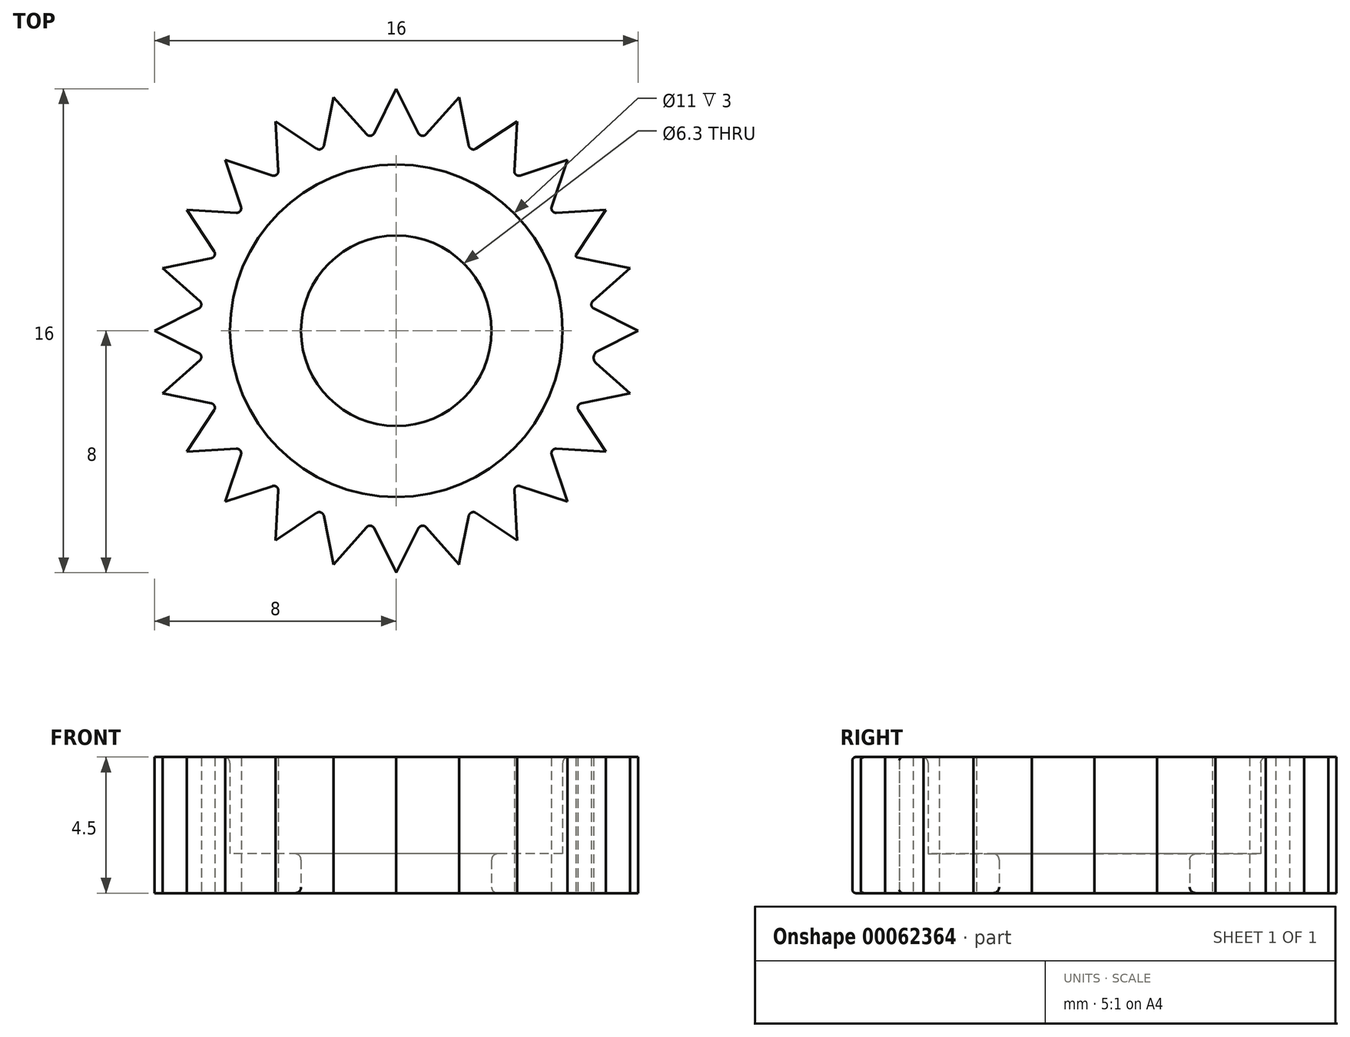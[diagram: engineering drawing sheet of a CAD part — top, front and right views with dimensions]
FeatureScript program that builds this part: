
annotation { "Feature Type Name" : "Feature", "Feature Type Description" : "" }
export const myFeature = defineFeature(function(context is Context, id is Id, definition is map)
    precondition{}
    {
        {
            var Q0;
            Q0=qCreatedBy(makeId("Top.planeOp"),FACE);
            var sketch = newSketch(context, id + "F0", { "sketchPlane" : qUnion([Q0])});
            skCircle(sketch, "E0", {"center": v(0, 0) * mm, "radius": 8 * mm, "construction": true});
            skCircle(sketch, "E1", {"center": v(0, 0) * mm, "radius": 6.5 * mm, "construction": true});
            skCircle(sketch, "E2", {"center": v(0, 0) * mm, "radius": 5.5 * mm});
            skCircle(sketch, "E3", {"center": v(0, 0) * mm, "radius": 3.15 * mm});
            skLineSegment(sketch, "E4", {"start": v(0, 6.5) * mm, "end": v(0.75, 6.5) * mm, "construction": true});
            skLineSegment(sketch, "E5", {"start": v(0.73, 6.53) * mm, "end": v(0, 8) * mm});
            skLineSegment(sketch, "E6", {"start": v(0, 8) * mm, "end": v(0, 6.5) * mm, "construction": true});
            skLineSegment(sketch, "E7.MirrorCS", {"start": v(-0.73, 6.53) * mm, "end": v(0, 8) * mm});
            skPoint(sketch, "E8.visualSharp", {"position": v(0, 8) * mm});
            skLineSegment(sketch, "E9.1.0", {"start": v(2.4, 6.12) * mm, "end": v(2.07, 7.73) * mm});
            skLineSegment(sketch, "E9.1.2", {"start": v(0.98, 6.5) * mm, "end": v(2.07, 7.73) * mm});
            skLineSegment(sketch, "E9.2.0", {"start": v(3.9, 5.29) * mm, "end": v(4, 6.93) * mm});
            skLineSegment(sketch, "E9.2.2", {"start": v(2.63, 6.02) * mm, "end": v(4, 6.93) * mm});
            skLineSegment(sketch, "E9.3.0", {"start": v(5.14, 4.1) * mm, "end": v(5.66, 5.66) * mm});
            skLineSegment(sketch, "E9.3.2", {"start": v(4.1, 5.14) * mm, "end": v(5.66, 5.66) * mm});
            skLineSegment(sketch, "E9.4.0", {"start": v(5.94, 2.5) * mm, "end": v(6.93, 4) * mm});
            skLineSegment(sketch, "E9.4.2", {"start": v(5.29, 3.9) * mm, "end": v(6.93, 4) * mm});
            skLineSegment(sketch, "E9.5.0", {"start": v(6.5, 0.98) * mm, "end": v(7.73, 2.07) * mm});
            skLineSegment(sketch, "E9.5.1", {"start": v(7.5, 1.87) * mm, "end": v(7.5, 1.87) * mm});
            skLineSegment(sketch, "E9.5.2", {"start": v(5.97, 2.43) * mm, "end": v(7.73, 2.07) * mm});
            skLineSegment(sketch, "E9.6.0", {"start": v(6.66, -0.67) * mm, "end": v(8, 0) * mm});
            skLineSegment(sketch, "E9.6.1", {"start": v(7.73, -0.13) * mm, "end": v(7.73, -0.13) * mm});
            skLineSegment(sketch, "E9.6.2", {"start": v(6.53, 0.73) * mm, "end": v(8, 0) * mm});
            skLineSegment(sketch, "E9.7.0", {"start": v(6.12, -2.4) * mm, "end": v(7.73, -2.07) * mm});
            skLineSegment(sketch, "E9.7.2", {"start": v(6.6, -1.08) * mm, "end": v(7.73, -2.07) * mm});
            skLineSegment(sketch, "E9.8.0", {"start": v(5.29, -3.9) * mm, "end": v(6.93, -4) * mm});
            skLineSegment(sketch, "E9.8.2", {"start": v(6.02, -2.63) * mm, "end": v(6.93, -4) * mm});
            skLineSegment(sketch, "E9.9.0", {"start": v(4.1, -5.14) * mm, "end": v(5.66, -5.66) * mm});
            skLineSegment(sketch, "E9.9.2", {"start": v(5.14, -4.1) * mm, "end": v(5.66, -5.66) * mm});
            skLineSegment(sketch, "E9.10.0", {"start": v(2.63, -6.02) * mm, "end": v(4, -6.93) * mm});
            skLineSegment(sketch, "E9.10.2", {"start": v(3.9, -5.29) * mm, "end": v(4, -6.93) * mm});
            skLineSegment(sketch, "E9.11.0", {"start": v(0.98, -6.5) * mm, "end": v(2.07, -7.73) * mm});
            skLineSegment(sketch, "E9.11.2", {"start": v(2.4, -6.12) * mm, "end": v(2.07, -7.73) * mm});
            skLineSegment(sketch, "E9.12.0", {"start": v(-0.73, -6.53) * mm, "end": v(0, -8) * mm});
            skLineSegment(sketch, "E9.12.1", {"start": v(-0.13, -7.73) * mm, "end": v(-0.13, -7.73) * mm});
            skLineSegment(sketch, "E9.12.2", {"start": v(0.73, -6.53) * mm, "end": v(0, -8) * mm});
            skLineSegment(sketch, "E9.13.0", {"start": v(-2.4, -6.12) * mm, "end": v(-2.07, -7.73) * mm});
            skLineSegment(sketch, "E9.13.2", {"start": v(-0.98, -6.5) * mm, "end": v(-2.07, -7.73) * mm});
            skLineSegment(sketch, "E9.14.0", {"start": v(-3.9, -5.29) * mm, "end": v(-4, -6.93) * mm});
            skLineSegment(sketch, "E9.14.2", {"start": v(-2.63, -6.02) * mm, "end": v(-4, -6.93) * mm});
            skLineSegment(sketch, "E9.15.0", {"start": v(-5.14, -4.1) * mm, "end": v(-5.66, -5.66) * mm});
            skLineSegment(sketch, "E9.15.2", {"start": v(-4.1, -5.14) * mm, "end": v(-5.66, -5.66) * mm});
            skLineSegment(sketch, "E9.16.0", {"start": v(-6.02, -2.63) * mm, "end": v(-6.93, -4) * mm});
            skLineSegment(sketch, "E9.16.1", {"start": v(-6.76, -3.75) * mm, "end": v(-6.76, -3.75) * mm});
            skLineSegment(sketch, "E9.16.2", {"start": v(-5.29, -3.9) * mm, "end": v(-6.93, -4) * mm});
            skLineSegment(sketch, "E9.17.0", {"start": v(-6.5, -0.98) * mm, "end": v(-7.73, -2.07) * mm});
            skLineSegment(sketch, "E9.17.1", {"start": v(-7.5, -1.87) * mm, "end": v(-7.5, -1.87) * mm});
            skLineSegment(sketch, "E9.17.2", {"start": v(-6.12, -2.4) * mm, "end": v(-7.73, -2.07) * mm});
            skLineSegment(sketch, "E9.18.0", {"start": v(-6.53, 0.73) * mm, "end": v(-8, 0) * mm});
            skLineSegment(sketch, "E9.18.2", {"start": v(-6.53, -0.73) * mm, "end": v(-8, 0) * mm});
            skLineSegment(sketch, "E9.19.0", {"start": v(-6.12, 2.4) * mm, "end": v(-7.73, 2.07) * mm});
            skLineSegment(sketch, "E9.19.2", {"start": v(-6.5, 0.98) * mm, "end": v(-7.73, 2.07) * mm});
            skLineSegment(sketch, "E9.20.0", {"start": v(-5.29, 3.9) * mm, "end": v(-6.93, 4) * mm});
            skLineSegment(sketch, "E9.20.2", {"start": v(-6.02, 2.63) * mm, "end": v(-6.93, 4) * mm});
            skLineSegment(sketch, "E9.21.0", {"start": v(-4.1, 5.14) * mm, "end": v(-5.66, 5.66) * mm});
            skLineSegment(sketch, "E9.21.2", {"start": v(-5.14, 4.1) * mm, "end": v(-5.66, 5.66) * mm});
            skLineSegment(sketch, "E9.22.0", {"start": v(-2.63, 6.02) * mm, "end": v(-4, 6.93) * mm});
            skLineSegment(sketch, "E9.22.2", {"start": v(-3.9, 5.29) * mm, "end": v(-4, 6.93) * mm});
            skLineSegment(sketch, "E9.23.0", {"start": v(-0.98, 6.5) * mm, "end": v(-2.07, 7.73) * mm});
            skLineSegment(sketch, "E9.23.2", {"start": v(-2.4, 6.12) * mm, "end": v(-2.07, 7.73) * mm});
            skLineSegment(sketch, "E9.anchor1", {"start": v(0, 0) * mm, "end": v(0.75, 6.5) * mm, "construction": true});
            skLineSegment(sketch, "E9.anchor2", {"start": v(0, 0) * mm, "end": v(-0.96, 6.47) * mm, "construction": true});
            skPoint(sketch, "E10.newPointA", {"position": v(0.75, 6.5) * mm});
            skPoint(sketch, "E10.newPointB", {"position": v(0.96, 6.47) * mm});
            skArc(sketch, "E10.filletArc", {"start": v(0.73, 6.53) * mm, "mid": v(0.85, 6.45) * mm, "end": v(0.98, 6.5) * mm});
            skPoint(sketch, "E11.newPointA", {"position": v(2.4, 6.08) * mm});
            skPoint(sketch, "E11.newPointB", {"position": v(2.6, 6) * mm});
            skArc(sketch, "E11.filletArc", {"start": v(2.4, 6.12) * mm, "mid": v(2.49, 6) * mm, "end": v(2.63, 6.02) * mm});
            skPoint(sketch, "E12.newPointA", {"position": v(3.9, 5.25) * mm});
            skPoint(sketch, "E12.newPointB", {"position": v(4.07, 5.13) * mm});
            skArc(sketch, "E12.filletArc", {"start": v(3.9, 5.29) * mm, "mid": v(3.96, 5.16) * mm, "end": v(4.1, 5.14) * mm});
            skPoint(sketch, "E13.newPointA", {"position": v(5.25, 3.9) * mm});
            skPoint(sketch, "E13.newPointB", {"position": v(5.13, 4.07) * mm});
            skArc(sketch, "E13.filletArc", {"start": v(5.14, 4.1) * mm, "mid": v(5.16, 3.96) * mm, "end": v(5.29, 3.9) * mm});
            skPoint(sketch, "E14.newPointA", {"position": v(6, 2.6) * mm});
            skPoint(sketch, "E14.newPointB", {"position": v(6.08, 2.4) * mm});
            skArc(sketch, "E14.filletArc", {"start": v(5.94, 2.5) * mm, "mid": v(5.94, 2.46) * mm, "end": v(5.97, 2.43) * mm});
            skPoint(sketch, "E15.newPointA", {"position": v(6.47, 0.96) * mm});
            skPoint(sketch, "E15.newPointB", {"position": v(6.5, 0.75) * mm});
            skArc(sketch, "E15.filletArc", {"start": v(6.5, 0.98) * mm, "mid": v(6.45, 0.85) * mm, "end": v(6.53, 0.73) * mm});
            skPoint(sketch, "E16.newPointA", {"position": v(6.5, -0.75) * mm});
            skPoint(sketch, "E16.newPointB", {"position": v(6.47, -0.96) * mm});
            skArc(sketch, "E16.filletArc", {"start": v(6.66, -0.67) * mm, "mid": v(6.53, -0.86) * mm, "end": v(6.6, -1.08) * mm});
            skPoint(sketch, "E17.newPointA", {"position": v(6.08, -2.4) * mm});
            skPoint(sketch, "E17.newPointB", {"position": v(6, -2.6) * mm});
            skArc(sketch, "E17.filletArc", {"start": v(6.12, -2.4) * mm, "mid": v(6, -2.49) * mm, "end": v(6.02, -2.63) * mm});
            skPoint(sketch, "E18.newPointA", {"position": v(5.56, -5.37) * mm});
            skPoint(sketch, "E18.newPointB", {"position": v(5.37, -5.56) * mm});
            skPoint(sketch, "E19.newPointA", {"position": v(2.6, -6) * mm});
            skPoint(sketch, "E19.newPointB", {"position": v(2.4, -6.08) * mm});
            skArc(sketch, "E19.filletArc", {"start": v(2.63, -6.02) * mm, "mid": v(2.49, -6) * mm, "end": v(2.4, -6.12) * mm});
            skPoint(sketch, "E20.newPointA", {"position": v(0.75, -6.5) * mm});
            skPoint(sketch, "E20.newPointB", {"position": v(0.96, -6.47) * mm});
            skArc(sketch, "E20.filletArc", {"start": v(0.98, -6.5) * mm, "mid": v(0.85, -6.45) * mm, "end": v(0.73, -6.53) * mm});
            skPoint(sketch, "E21.newPointA", {"position": v(3.9, -5.25) * mm});
            skPoint(sketch, "E21.newPointB", {"position": v(4.07, -5.13) * mm});
            skArc(sketch, "E21.filletArc", {"start": v(4.1, -5.14) * mm, "mid": v(3.96, -5.16) * mm, "end": v(3.9, -5.29) * mm});
            skPoint(sketch, "E22.newPointA", {"position": v(-0.96, -6.47) * mm});
            skPoint(sketch, "E22.newPointB", {"position": v(-0.75, -6.5) * mm});
            skArc(sketch, "E22.filletArc", {"start": v(-0.73, -6.53) * mm, "mid": v(-0.85, -6.45) * mm, "end": v(-0.98, -6.5) * mm});
            skPoint(sketch, "E23.newPointA", {"position": v(-2.6, -6) * mm});
            skPoint(sketch, "E23.newPointB", {"position": v(-2.4, -6.08) * mm});
            skArc(sketch, "E23.filletArc", {"start": v(-2.4, -6.12) * mm, "mid": v(-2.49, -6) * mm, "end": v(-2.63, -6.02) * mm});
            skPoint(sketch, "E24.newPointA", {"position": v(-4.07, -5.13) * mm});
            skPoint(sketch, "E24.newPointB", {"position": v(-3.9, -5.25) * mm});
            skArc(sketch, "E24.filletArc", {"start": v(-3.9, -5.29) * mm, "mid": v(-3.96, -5.16) * mm, "end": v(-4.1, -5.14) * mm});
            skPoint(sketch, "E25.newPointA", {"position": v(-5.25, -3.9) * mm});
            skPoint(sketch, "E25.newPointB", {"position": v(-5.13, -4.07) * mm});
            skArc(sketch, "E25.filletArc", {"start": v(-5.14, -4.1) * mm, "mid": v(-5.16, -3.96) * mm, "end": v(-5.29, -3.9) * mm});
            skPoint(sketch, "E26.newPointA", {"position": v(-6.08, -2.4) * mm});
            skPoint(sketch, "E26.newPointB", {"position": v(-6, -2.6) * mm});
            skArc(sketch, "E26.filletArc", {"start": v(-6.02, -2.63) * mm, "mid": v(-6, -2.49) * mm, "end": v(-6.12, -2.4) * mm});
            skPoint(sketch, "E27.newPointA", {"position": v(-6.5, -0.75) * mm});
            skPoint(sketch, "E27.newPointB", {"position": v(-6.47, -0.96) * mm});
            skArc(sketch, "E27.filletArc", {"start": v(-6.5, -0.98) * mm, "mid": v(-6.45, -0.85) * mm, "end": v(-6.53, -0.73) * mm});
            skPoint(sketch, "E28.newPointA", {"position": v(-6.47, 0.96) * mm});
            skPoint(sketch, "E28.newPointB", {"position": v(-6.5, 0.75) * mm});
            skArc(sketch, "E28.filletArc", {"start": v(-6.53, 0.73) * mm, "mid": v(-6.45, 0.85) * mm, "end": v(-6.5, 0.98) * mm});
            skPoint(sketch, "E29.newPointA", {"position": v(-6, 2.6) * mm});
            skPoint(sketch, "E29.newPointB", {"position": v(-6.08, 2.4) * mm});
            skArc(sketch, "E29.filletArc", {"start": v(-6.12, 2.4) * mm, "mid": v(-6, 2.49) * mm, "end": v(-6.02, 2.63) * mm});
            skPoint(sketch, "E30.newPointA", {"position": v(-5.13, 4.07) * mm});
            skPoint(sketch, "E30.newPointB", {"position": v(-5.25, 3.9) * mm});
            skArc(sketch, "E30.filletArc", {"start": v(-5.29, 3.9) * mm, "mid": v(-5.16, 3.96) * mm, "end": v(-5.14, 4.1) * mm});
            skPoint(sketch, "E31.newPointA", {"position": v(-4.07, 5.13) * mm});
            skPoint(sketch, "E31.newPointB", {"position": v(-3.9, 5.25) * mm});
            skArc(sketch, "E31.filletArc", {"start": v(-4.1, 5.14) * mm, "mid": v(-3.96, 5.16) * mm, "end": v(-3.9, 5.29) * mm});
            skPoint(sketch, "E32.newPointA", {"position": v(-2.6, 6) * mm});
            skPoint(sketch, "E32.newPointB", {"position": v(-2.4, 6.08) * mm});
            skArc(sketch, "E32.filletArc", {"start": v(-2.63, 6.02) * mm, "mid": v(-2.49, 6) * mm, "end": v(-2.4, 6.12) * mm});
            skPoint(sketch, "E33.newPointA", {"position": v(-0.96, 6.47) * mm});
            skPoint(sketch, "E33.newPointB", {"position": v(-0.75, 6.5) * mm});
            skArc(sketch, "E33.filletArc", {"start": v(-0.98, 6.5) * mm, "mid": v(-0.85, 6.45) * mm, "end": v(-0.73, 6.53) * mm});
            skPoint(sketch, "E34.newPointA", {"position": v(5.13, -4.07) * mm});
            skPoint(sketch, "E34.newPointB", {"position": v(5.25, -3.9) * mm});
            skArc(sketch, "E34.filletArc", {"start": v(5.29, -3.9) * mm, "mid": v(5.16, -3.96) * mm, "end": v(5.14, -4.1) * mm});
            skPoint(sketch, "E35.orphan", {"position": v(-6.63, 3.98) * mm});
            skPoint(sketch, "E36.orphan", {"position": v(-6.76, 3.75) * mm});
            skPoint(sketch, "E37.orphan", {"position": v(-5.56, 5.37) * mm});
            skPoint(sketch, "E38.orphan", {"position": v(-5.37, 5.56) * mm});
            skPoint(sketch, "E39.orphan", {"position": v(-3.98, 6.63) * mm});
            skPoint(sketch, "E40.orphan", {"position": v(-3.75, 6.76) * mm});
            skPoint(sketch, "E41.orphan", {"position": v(-7.43, -2.13) * mm});
            skPoint(sketch, "E42.orphan", {"position": v(-7.73, -0.13) * mm});
            skPoint(sketch, "E43.orphan", {"position": v(-7.73, 0.13) * mm});
            skPoint(sketch, "E44.orphan", {"position": v(-7.5, 1.87) * mm});
            skPoint(sketch, "E45.orphan", {"position": v(-7.43, 2.13) * mm});
            skPoint(sketch, "E46.orphan", {"position": v(-6.63, -3.98) * mm});
            skPoint(sketch, "E47.orphan", {"position": v(-5.56, -5.37) * mm});
            skPoint(sketch, "E48.orphan", {"position": v(-5.37, -5.56) * mm});
            skPoint(sketch, "E49.orphan", {"position": v(-3.98, -6.63) * mm});
            skPoint(sketch, "E50.orphan", {"position": v(-3.75, -6.76) * mm});
            skPoint(sketch, "E51.orphan", {"position": v(-2.13, 7.43) * mm});
            skPoint(sketch, "E52.orphan", {"position": v(-1.87, 7.5) * mm});
            skPoint(sketch, "E53.orphan", {"position": v(-0.13, 7.73) * mm});
            skPoint(sketch, "E54.orphan", {"position": v(0.13, 7.73) * mm});
            skPoint(sketch, "E55.orphan", {"position": v(1.87, 7.5) * mm});
            skPoint(sketch, "E56.orphan", {"position": v(2.13, 7.43) * mm});
            skPoint(sketch, "E57.orphan", {"position": v(3.98, 6.63) * mm});
            skPoint(sketch, "E58.orphan", {"position": v(3.75, 6.76) * mm});
            skPoint(sketch, "E59.orphan", {"position": v(5.37, 5.56) * mm});
            skPoint(sketch, "E60.orphan", {"position": v(5.56, 5.37) * mm});
            skPoint(sketch, "E61.orphan", {"position": v(6.63, 3.98) * mm});
            skPoint(sketch, "E62.orphan", {"position": v(6.76, 3.75) * mm});
            skPoint(sketch, "E63.orphan", {"position": v(7.43, 2.13) * mm});
            skPoint(sketch, "E64.orphan", {"position": v(7.73, 0.13) * mm});
            skPoint(sketch, "E65.orphan", {"position": v(7.5, -1.87) * mm});
            skPoint(sketch, "E66.orphan", {"position": v(7.43, -2.13) * mm});
            skPoint(sketch, "E67.orphan", {"position": v(6.63, -3.98) * mm});
            skPoint(sketch, "E68.orphan", {"position": v(6.76, -3.75) * mm});
            skPoint(sketch, "E69.orphan", {"position": v(3.98, -6.63) * mm});
            skPoint(sketch, "E70.orphan", {"position": v(3.75, -6.76) * mm});
            skPoint(sketch, "E71.orphan", {"position": v(1.87, -7.5) * mm});
            skPoint(sketch, "E72.orphan", {"position": v(2.13, -7.43) * mm});
            skPoint(sketch, "E73.orphan", {"position": v(0.13, -7.73) * mm});
            skPoint(sketch, "E74.orphan", {"position": v(-1.87, -7.5) * mm});
            skPoint(sketch, "E75.orphan", {"position": v(-2.13, -7.43) * mm});
            skSolve(sketch);
        }
        {
            var Q0;
            Q0=makeQuery(id+"F0.imprint","IMPRINT",FACE,{"disambiguationData":[TD([[makeQuery(id+"F0.imprint","IMPRINT",EDGE,{"derivedFrom":sQuery(id+"F0.wireOp",EDGE,"E2")}),-1.0]])]});
            var Q1;
            Q1=sQuery(id+"F0.wireOp",EDGE,"E1");
            extrude(context, id + "F1", {"entities" : qUnion([Q0]), "surfaceEntities" : qUnion([Q1]), "depth" : 4.5 * mm});
        }
        {
            var Q0;
            Q0=makeQuery(id+"F0.imprint","IMPRINT",FACE,{"disambiguationData":[TD([[makeQuery(id+"F0.imprint","IMPRINT",EDGE,{"derivedFrom":sQuery(id+"F0.wireOp",EDGE,"E2")}),1.0]])]});
            extrude(context, id + "F2", {"entities" : qUnion([Q0]), "operationType" : NewBodyOperationType.ADD, "depth" : 1.3 * mm});
        }
        {
            var Q0;
            Q0=makeQuery(id+"F2.opExtrude","CAP_EDGE",EDGE,{"disambiguationData":[OSD([sQuery(id+"F0.wireOp",EDGE,"E3")])],"isStart":false});
            var Q1;
            Q1=makeQuery(id+"F2.opExtrude","CAP_EDGE",EDGE,{"disambiguationData":[OSD([sQuery(id+"F0.wireOp",EDGE,"E2")])],"isStart":false});
            var Q2;
            Q2=makeQuery(id+"F1.opExtrude","CAP_EDGE",EDGE,{"disambiguationData":[OSD([sQuery(id+"F0.wireOp",EDGE,"E2")])],"isStart":false});
            var Q3;
            Q3=makeQuery(id+"F2.opExtrude","CAP_EDGE",EDGE,{"disambiguationData":[OSD([sQuery(id+"F0.wireOp",EDGE,"E3")])],"isStart":true});
            fillet(context, id + "F3", {"entities" : qUnion([Q0, Q1, Q2, Q3]), "radius" : 0.2 * mm, "tangentPropagation" : true, "allowEdgeOverflow" : false});
        }
        {
            var Q0;
            Q0=makeQuery(id+"F1.opExtrude","CAP_EDGE",EDGE,{"disambiguationData":[OSD([sQuery(id+"F0.wireOp",EDGE,"E9.12.2")])],"isStart":false});
            var Q1;
            Q1=makeQuery(id+"F1.opExtrude","CAP_EDGE",EDGE,{"disambiguationData":[OSD([sQuery(id+"F0.wireOp",EDGE,"E9.12.2")])],"isStart":true});
            fillet(context, id + "F4", {"entities" : qUnion([Q0, Q1]), "radius" : 0.1 * mm, "tangentPropagation" : true, "allowEdgeOverflow" : false});
        }
    });
